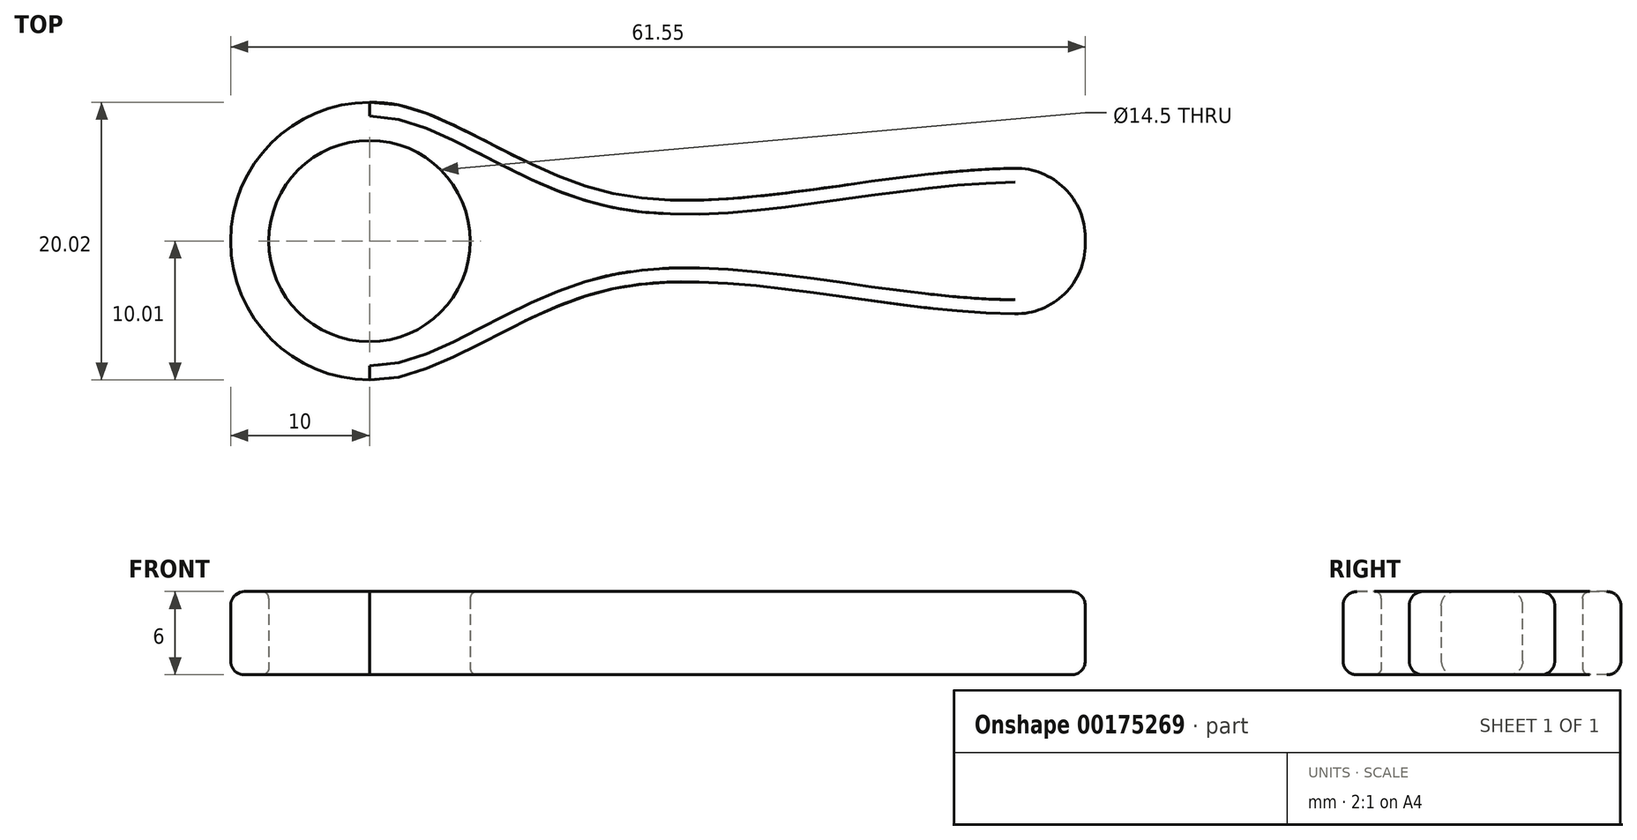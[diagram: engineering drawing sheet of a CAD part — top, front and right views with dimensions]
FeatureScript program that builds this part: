
annotation { "Feature Type Name" : "Feature", "Feature Type Description" : "" }
export const myFeature = defineFeature(function(context is Context, id is Id, definition is map)
    precondition{}
    {
        {
            var Q0;
            Q0=qCreatedBy(makeId("Top.planeOp"),FACE);
            var sketch = newSketch(context, id + "F0", { "sketchPlane" : qUnion([Q0])});
            skCircle(sketch, "E0", {"center": v(0, 0) * mm, "radius": 7.25 * mm});
            skCircle(sketch, "E1", {"center": v(0, 0) * mm, "radius": 10 * mm});
            skLineSegment(sketch, "E2", {"start": v(51.55, 5) * mm, "end": v(51.55, -5) * mm});
            skFitSpline(sketch, "E3", {"points": [v(0, -10) * mm, v(17.7, -3.4) * mm, v(51.55, -5) * mm], "startDerivative": vector(36.28, -1.37) * mm, "endDerivative": vector(60.97, 7.22) * mm});
            skFitSpline(sketch, "E4.MirrorCS", {"points": [v(0, 10) * mm, v(17.7, 3.4) * mm, v(51.55, 5) * mm], "startDerivative": vector(36.28, 1.37) * mm, "endDerivative": vector(60.97, -7.22) * mm});
            skSolve(sketch);
        }
        {
            var Q0;
            Q0 = qSketchRegion(id + "F0", true);
            extrude(context, id + "F1", {"entities" : qUnion([Q0]), "depth" : 6 * mm});
        }
        {
            var Q0;
            Q0=makeQuery(id+"F1.opExtrude","SWEPT_EDGE",EDGE,{"disambiguationData":[OSD([sQuery(id+"F0.wireOp",EDGE,"E2"),sQuery(id+"F0.wireOp",EDGE,"LiMI4g3x-Ub7L-HzqR-8dG1-9Mk6N0thp5We")])]});
            var Q1;
            Q1=makeQuery(id+"F1.opExtrude","SWEPT_EDGE",EDGE,{"disambiguationData":[OSD([sQuery(id+"F0.wireOp",EDGE,"KogE2yOf-XQ3Q-wfs9-vSaF-3sXPLG2ve2sv"),sQuery(id+"F0.wireOp",EDGE,"E2")])]});
            fillet(context, id + "F2", {"entities" : qUnion([Q0, Q1]), "radius" : 5 * mm, "tangentPropagation" : true, "allowEdgeOverflow" : false});
        }
        {
            var Q0;
            Q0=makeQuery(id+"F1.opExtrude","CAP_EDGE",EDGE,{"disambiguationData":[OSD([sQuery(id+"F0.wireOp",EDGE,"E1")])],"isStart":false});
            var Q1;
            Q1=makeQuery(id+"F1.opExtrude","CAP_EDGE",EDGE,{"disambiguationData":[OSD([sQuery(id+"F0.wireOp",EDGE,"KogE2yOf-XQ3Q-wfs9-vSaF-3sXPLG2ve2sv")])],"isStart":false});
            var Q2;
            Q2=makeQuery(id+"F1.opExtrude","CAP_EDGE",EDGE,{"disambiguationData":[OSD([sQuery(id+"F0.wireOp",EDGE,"LiMI4g3x-Ub7L-HzqR-8dG1-9Mk6N0thp5We")])],"isStart":false});
            var Q3;
            {var subQ0=sQuery(id+"F0.wireOp",EDGE,"LiMI4g3x-Ub7L-HzqR-8dG1-9Mk6N0thp5We");var subQ1=sQuery(id+"F0.wireOp",EDGE,"E2");Q3=makeQuery(id+"F2.opFillet","BLEND_EDGE",EDGE,{"blendedFrom":[makeQuery(id+"F1.opExtrude","SWEPT_EDGE",EDGE,{"disambiguationData":[OSD([subQ1,subQ0])]}),makeQuery(id+"F1.opExtrude","CAP_FACE",FACE,{"disambiguationData":[OSD([sQuery(id+"F0.wireOp",EDGE,"E0"),sQuery(id+"F0.wireOp",EDGE,"E1"),sQuery(id+"F0.wireOp",EDGE,"KogE2yOf-XQ3Q-wfs9-vSaF-3sXPLG2ve2sv"),subQ1,subQ0])],"isStart":false})],"blendedInto":[makeQuery(id+"F1.opExtrude","CAP_FACE",FACE,{"disambiguationData":[OSD([sQuery(id+"F0.wireOp",EDGE,"E0"),sQuery(id+"F0.wireOp",EDGE,"E1"),sQuery(id+"F0.wireOp",EDGE,"KogE2yOf-XQ3Q-wfs9-vSaF-3sXPLG2ve2sv"),subQ1,subQ0])],"isStart":false})]});}
            var Q4;
            {var subQ0=sQuery(id+"F0.wireOp",EDGE,"E2");var subQ1=sQuery(id+"F0.wireOp",EDGE,"KogE2yOf-XQ3Q-wfs9-vSaF-3sXPLG2ve2sv");Q4=makeQuery(id+"F2.opFillet","BLEND_EDGE",EDGE,{"blendedFrom":[makeQuery(id+"F1.opExtrude","SWEPT_EDGE",EDGE,{"disambiguationData":[OSD([subQ1,subQ0])]}),makeQuery(id+"F1.opExtrude","CAP_FACE",FACE,{"disambiguationData":[OSD([sQuery(id+"F0.wireOp",EDGE,"E0"),sQuery(id+"F0.wireOp",EDGE,"E1"),subQ1,subQ0,sQuery(id+"F0.wireOp",EDGE,"LiMI4g3x-Ub7L-HzqR-8dG1-9Mk6N0thp5We")])],"isStart":false})],"blendedInto":[makeQuery(id+"F1.opExtrude","CAP_FACE",FACE,{"disambiguationData":[OSD([sQuery(id+"F0.wireOp",EDGE,"E0"),sQuery(id+"F0.wireOp",EDGE,"E1"),subQ1,subQ0,sQuery(id+"F0.wireOp",EDGE,"LiMI4g3x-Ub7L-HzqR-8dG1-9Mk6N0thp5We")])],"isStart":false})]});}
            var Q5;
            Q5=makeQuery(id+"F1.opExtrude","CAP_EDGE",EDGE,{"disambiguationData":[OSD([sQuery(id+"F0.wireOp",EDGE,"E1")])],"isStart":true});
            var Q6;
            Q6=makeQuery(id+"F1.opExtrude","CAP_EDGE",EDGE,{"disambiguationData":[OSD([sQuery(id+"F0.wireOp",EDGE,"LiMI4g3x-Ub7L-HzqR-8dG1-9Mk6N0thp5We")])],"isStart":true});
            var Q7;
            {var subQ0=sQuery(id+"F0.wireOp",EDGE,"LiMI4g3x-Ub7L-HzqR-8dG1-9Mk6N0thp5We");var subQ1=sQuery(id+"F0.wireOp",EDGE,"E2");Q7=makeQuery(id+"F2.opFillet","BLEND_EDGE",EDGE,{"blendedFrom":[makeQuery(id+"F1.opExtrude","SWEPT_EDGE",EDGE,{"disambiguationData":[OSD([subQ1,subQ0])]}),makeQuery(id+"F1.opExtrude","CAP_FACE",FACE,{"disambiguationData":[OSD([sQuery(id+"F0.wireOp",EDGE,"E0"),sQuery(id+"F0.wireOp",EDGE,"E1"),sQuery(id+"F0.wireOp",EDGE,"KogE2yOf-XQ3Q-wfs9-vSaF-3sXPLG2ve2sv"),subQ1,subQ0])],"isStart":true})],"blendedInto":[makeQuery(id+"F1.opExtrude","CAP_FACE",FACE,{"disambiguationData":[OSD([sQuery(id+"F0.wireOp",EDGE,"E0"),sQuery(id+"F0.wireOp",EDGE,"E1"),sQuery(id+"F0.wireOp",EDGE,"KogE2yOf-XQ3Q-wfs9-vSaF-3sXPLG2ve2sv"),subQ1,subQ0])],"isStart":true})]});}
            var Q8;
            {var subQ0=sQuery(id+"F0.wireOp",EDGE,"E2");var subQ1=sQuery(id+"F0.wireOp",EDGE,"KogE2yOf-XQ3Q-wfs9-vSaF-3sXPLG2ve2sv");Q8=makeQuery(id+"F2.opFillet","BLEND_EDGE",EDGE,{"blendedFrom":[makeQuery(id+"F1.opExtrude","SWEPT_EDGE",EDGE,{"disambiguationData":[OSD([subQ1,subQ0])]}),makeQuery(id+"F1.opExtrude","CAP_FACE",FACE,{"disambiguationData":[OSD([sQuery(id+"F0.wireOp",EDGE,"E0"),sQuery(id+"F0.wireOp",EDGE,"E1"),subQ1,subQ0,sQuery(id+"F0.wireOp",EDGE,"LiMI4g3x-Ub7L-HzqR-8dG1-9Mk6N0thp5We")])],"isStart":true})],"blendedInto":[makeQuery(id+"F1.opExtrude","CAP_FACE",FACE,{"disambiguationData":[OSD([sQuery(id+"F0.wireOp",EDGE,"E0"),sQuery(id+"F0.wireOp",EDGE,"E1"),subQ1,subQ0,sQuery(id+"F0.wireOp",EDGE,"LiMI4g3x-Ub7L-HzqR-8dG1-9Mk6N0thp5We")])],"isStart":true})]});}
            var Q9;
            Q9=makeQuery(id+"F1.opExtrude","CAP_EDGE",EDGE,{"disambiguationData":[OSD([sQuery(id+"F0.wireOp",EDGE,"KogE2yOf-XQ3Q-wfs9-vSaF-3sXPLG2ve2sv")])],"isStart":true});
            fillet(context, id + "F3", {"entities" : qUnion([Q0, Q1, Q2, Q3, Q4, Q5, Q6, Q7, Q8, Q9]), "radius" : 1 * mm, "tangentPropagation" : true, "allowEdgeOverflow" : false});
        }
        {
            var Q0;
            Q0=makeQuery(id+"F1.opExtrude","CAP_EDGE",EDGE,{"disambiguationData":[OSD([sQuery(id+"F0.wireOp",EDGE,"E0")])],"isStart":true});
            fillet(context, id + "F4", {"entities" : qUnion([Q0]), "radius" : 0.5 * mm, "tangentPropagation" : true, "allowEdgeOverflow" : false});
        }
        {
            var Q0;
            Q0=makeQuery(id+"F1.opExtrude","CAP_EDGE",EDGE,{"disambiguationData":[OSD([sQuery(id+"F0.wireOp",EDGE,"E0")])],"isStart":false});
            fillet(context, id + "F5", {"entities" : qUnion([Q0]), "radius" : 0.5 * mm, "tangentPropagation" : true, "allowEdgeOverflow" : false});
        }
    });
